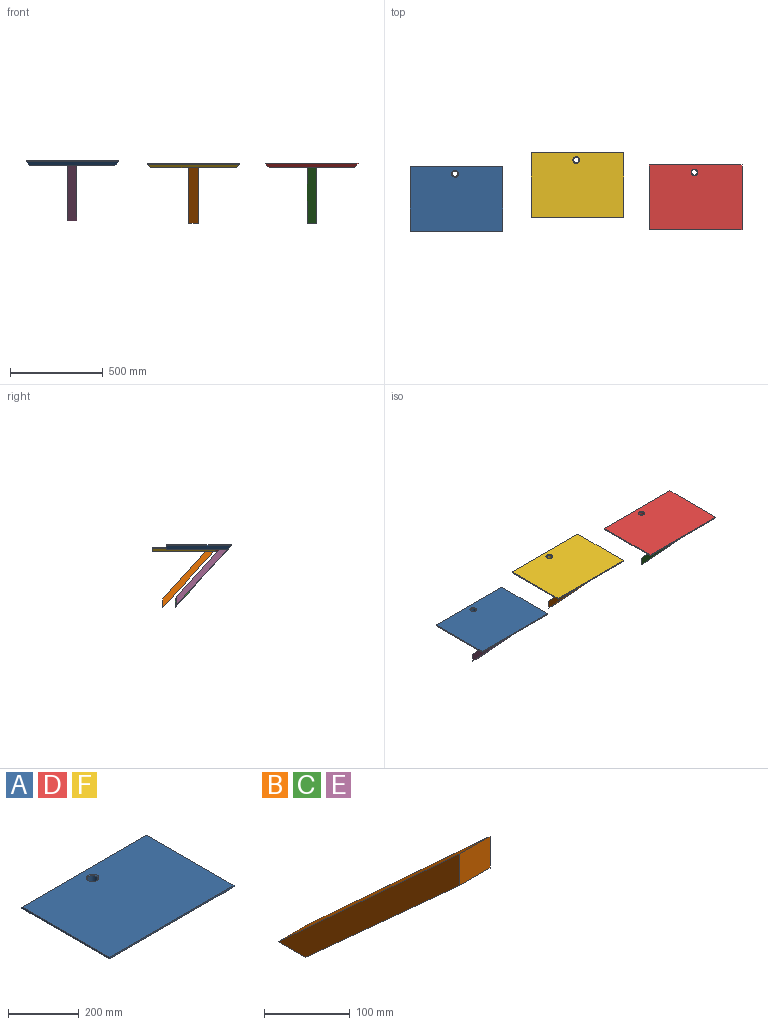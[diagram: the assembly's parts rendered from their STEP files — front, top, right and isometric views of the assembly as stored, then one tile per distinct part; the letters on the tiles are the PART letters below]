
ASSEMBLY  parts=6 mates=3
PART A: 12 faces, bbox 500x350x25 mm
  f0: plane 500x25mm, normal (0,1,0), area 12100mm2, adj f1,f4,f5,f6,f7,f9
  f1: plane 350x5mm, normal (-1,0,0), area 1750mm2, adj f0,f2,f5,f9
  f2: plane 500x5mm, normal (0,-1,0), area 2500mm2, adj f1,f4,f5,f8
  f3: cylinder r=15mm len=30mm, axis (0,0,-1), area 1790.7mm2, adj f10,f11
  f4: plane 350x5mm, normal (1,0,0), area 1750mm2, adj f0,f2,f5,f7
  f5: plane 500x350mm, normal (0,0,1), area 173982.1mm2, adj f0,f1,f2,f4,f11
  f6: plane 460x330mm, normal (0,0,-1), area 150782.1mm2, adj f0,f7,f8,f9,f10
  f7: plane 350x20mm, normal (0.71,0,-0.71), area 9616.7mm2, adj f0,f4,f6,f8
  f8: plane 500x20mm, normal (0,-0.71,-0.71), area 13576.5mm2, adj f2,f6,f7,f9
  f9: plane 350x20mm, normal (-0.71,0,-0.71), area 9616.7mm2, adj f0,f1,f6,f8
  f10: cone r=18mm half-angle=45deg, axis (0,0,-1), area 439.8mm2, adj f3,f6
  f11: cone r=15mm half-angle=45deg, axis (0,0,1), area 439.8mm2, adj f3,f5
PART B: 6 faces, bbox 50x300x275.4 mm
  f0: plane 50x45mm, normal (0,0,-1), area 2250mm2, adj f1,f3,f4,f5
  f1: plane 300.01x275.39mm, normal (0,0.68,0.74), area 20361.8mm2, adj f0,f2,f4,f5
  f2: plane 50x45mm, normal (0,-1,0), area 2250mm2, adj f1,f3,f4,f5
  f3: plane 255.01x230.39mm, normal (0,-0.67,-0.74), area 17183.2mm2, adj f0,f2,f4,f5
  f4: plane 300.01x275.39mm, normal (1,0,0), area 11933.8mm2, adj f0,f1,f2,f3
  f5: plane 300.01x275.39mm, normal (-1,0,0), area 11933.8mm2, adj f0,f1,f2,f3
PART C: same geometry as B
PART D: same geometry as A
PART E: same geometry as B
PART F: same geometry as A
PLACE A t=(-944.86,-115.54,-16.31)mm
PLACE B rot(axis=(0,-0.71,0.71),180deg) t=(-258.13,117.34,-329.38)mm
PLACE C rot(axis=(0,-0.71,0.71),180deg) t=(380.08,51.02,-328.98)mm
PLACE D t=(348.05,-107.46,-28.97)mm
PLACE E rot(axis=(0,-0.71,0.71),180deg) t=(-912.82,42.94,-316.32)mm
PLACE F t=(-290.16,-41.14,-29.38)mm
MATE fastened B.f2 <-> F.f6  axis (0,0,1) through (-283.13,-158.04,-29.38)mm
MATE fastened C.f2 <-> D.f6  axis (0,0,1) through (355.08,-224.37,-28.97)mm
MATE fastened E.f2 <-> A.f6  axis (0,0,1) through (-937.82,-232.44,-16.31)mm
